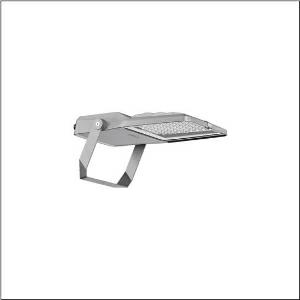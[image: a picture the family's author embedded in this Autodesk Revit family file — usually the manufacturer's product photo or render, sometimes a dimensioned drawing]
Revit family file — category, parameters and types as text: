
# Revit family: floodlight_fl_21_mini___pl33t_5xa7772c3f1a_c1da
name_source: partatom
category: Lighting Fixtures
units: mm (PartAtom-declared; Revit-internal decimal feet)

## family parameters
Cut with Voids When Loaded = No
Host = Face
Light Source = No
Part Type = Normal
Room Calculation Point = No
Round Connector Dimension = Use Diameter
Shared = No

## types (1)
- --- (1 x LED, 10390 lm, 87.2 W, 3000K)
    Apparent Load = 87 VA
    CIE Flux Codes = 26 75 99 100 100
    Color Rendering = 80
    Color Temperature = 3000K
    Default Elevation = 1800 mm
    Description = Floodlight FL 21 mini, floodlight, primary light control with lens, of PMMA, primary optical cover: protective disc, of toughened safety glass, transparent, light distribution: PL33T, light emission: direct distribution, installation type: surface-mounted, LED, High Power LED, rated luminous flux: 10.390lm, luminous efficacy: 119lm/W, light colour: 830, colour temperature: 3000K, control gear: ECG iQ, control: Street-Remote, Auto-Match, Temp-Guard, Night-Set, Smart-Wire, Desk-Remote (wireless, voltage-free reading and setting of iQ features in the workshop via application-optimized NFC function/RFID function), optimised constant luminous flux control (CLO 2.0), with terminal, 6-pole, mains connection: 220..240V, AC, 50/60Hz, start of lifetime: 87W, end of lifetime: 92W, reduction: 40W, luminaire housing, of diecast aluminium, powder-coated, Siteco® metallic grey (DB 702S), corrosivity category C5 according to DIN EN ISO 12944, mounting bracket, of steel, galvanised, powder-coated, Siteco® metallic grey (DB 702S), protection rating (complete): IP66, insulation class (complete): insulation class II (safety insulation), certification: CE, ENEC, VDE, protection symbol: D, impact resistance: IK08, permissible operating ambient temperature: -40..+40°C, permissible operating ambient temperature for outdoor applications: -40..+50°C, standard: DIN EN 12944, packaging unit: 1 piece

Light Distribution: PL33T
    Height = 70 mm
    Lamp = 1 x LED
    Lamp Light Flux = 10390 lm
    Lamp Power = 87.2 W
    Lamp count = 1
    Length = 485 mm
    Luminous efficacy = 119 lm/W
    Manufacturer = Siteco
    ModVariant = No
    Model = 5XA7772C3F1A
    Number of Poles = 1
    OnlyDefault = Yes
    Power Factor = 1
    Product Name = Floodlight FL 21 mini | PL33T
    Product group = floodlight | pylon top
    ProductGroupID = 6101
    Protection Class = Protection class II
    Protection Degree = IP 66
    RLX_Detail_Level = 1
    RlxData = <blob elided: 96129 chars, md5=19275522>
    Socket = socket
    Standby Power = 0 W
    System Light Flux = 10390 lm
    System Power = 87 W
    Type Comments = factory setting: luminous flux: 100 % | dim-lin: 254 | 456 mA
    Type Image = l_1006845.jpg
    URL = http://relux.com
    VarID = @adj_059477
    Voltage = 0 V
    Weight = 0.00 kg
    Width = 337 mm

## geometry (parser evidence)
native form markers: Blend x4, Sweep x12
no freeform markers — native parametric forms only
